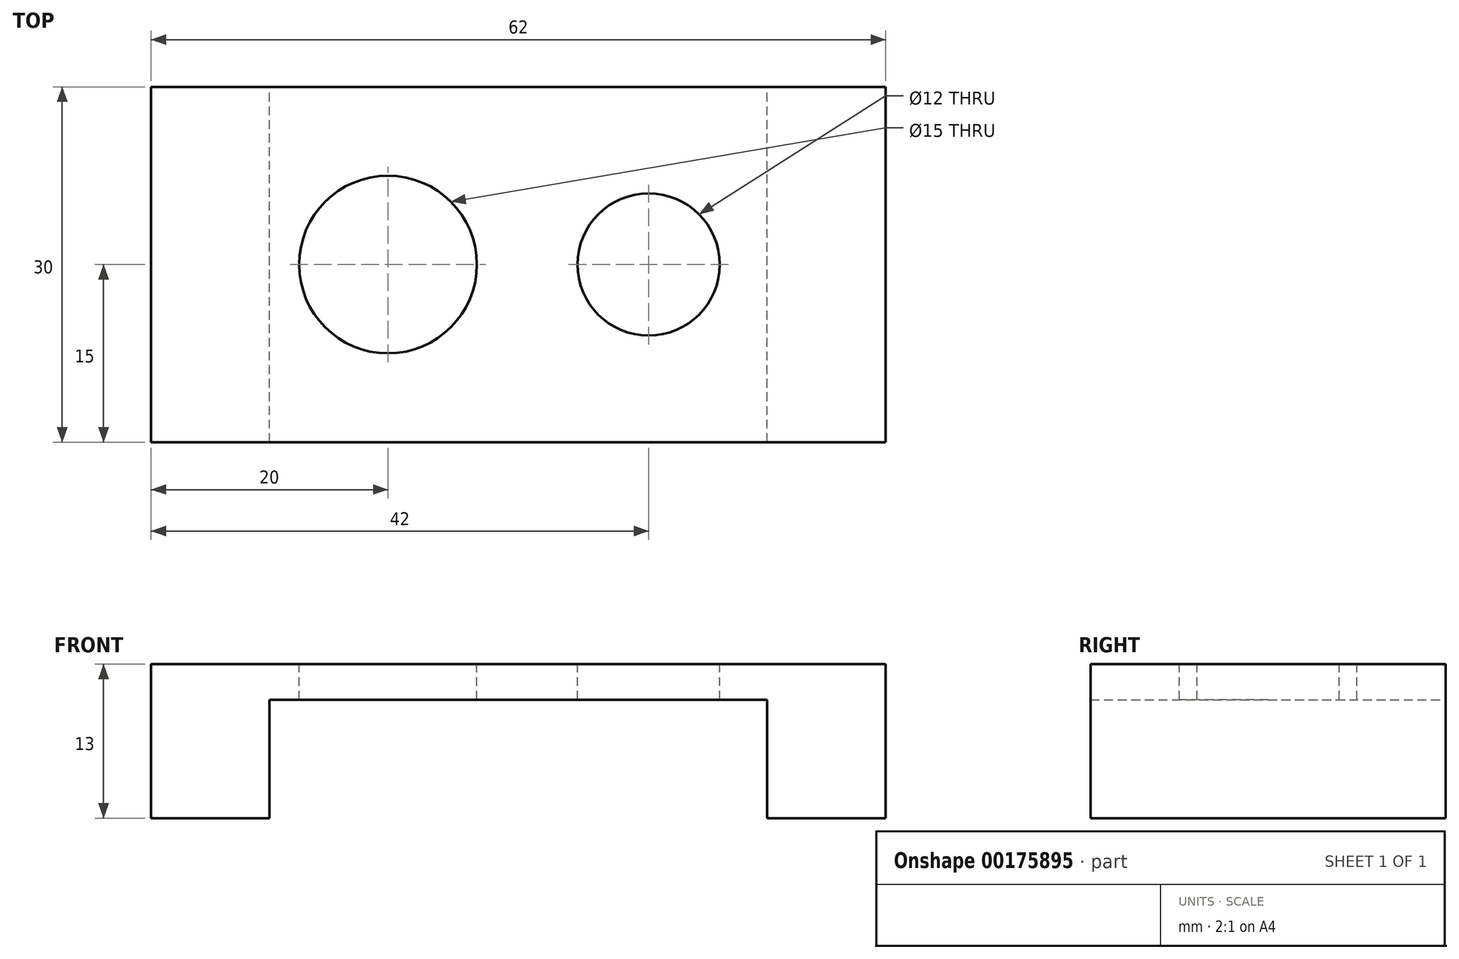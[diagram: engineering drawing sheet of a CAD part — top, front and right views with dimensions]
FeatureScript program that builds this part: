
annotation { "Feature Type Name" : "Feature", "Feature Type Description" : "" }
export const myFeature = defineFeature(function(context is Context, id is Id, definition is map)
    precondition{}
    {
        {
            var Q0;
            Q0=qCreatedBy(makeId("Front.planeOp"),FACE);
            var sketch = newSketch(context, id + "F0", { "sketchPlane" : qUnion([Q0])});
            skLineSegment(sketch, "E0", {"start": v(0, 0) * mm, "end": v(62, 0) * mm});
            skLineSegment(sketch, "E1", {"start": v(62, 0) * mm, "end": v(62, -13) * mm});
            skLineSegment(sketch, "E2", {"start": v(62, -13) * mm, "end": v(52, -13) * mm});
            skLineSegment(sketch, "E3", {"start": v(52, -13) * mm, "end": v(52, -3) * mm});
            skLineSegment(sketch, "E4", {"start": v(52, -3) * mm, "end": v(10, -3) * mm});
            skLineSegment(sketch, "E5", {"start": v(10, -3) * mm, "end": v(10, -13) * mm});
            skLineSegment(sketch, "E6", {"start": v(10, -13) * mm, "end": v(0, -13) * mm});
            skLineSegment(sketch, "E7", {"start": v(0, -13) * mm, "end": v(0, 0) * mm});
            skSolve(sketch);
        }
        {
            var Q0;
            Q0 = qSketchRegion(id + "F0", true);
            extrude(context, id + "F1", {"entities" : qUnion([Q0]), "depth" : 30 * mm});
        }
        {
            var Q0;
            Q0=qCreatedBy(makeId("Top.planeOp"),FACE);
            var sketch = newSketch(context, id + "F2", { "sketchPlane" : qUnion([Q0])});
            skCircle(sketch, "E8", {"center": v(20, -15) * mm, "radius": 7.5 * mm});
            skCircle(sketch, "E9", {"center": v(42, -15) * mm, "radius": 6 * mm});
            skSolve(sketch);
        }
        {
            var Q0;
            Q0 = qSketchRegion(id + "F2", true);
            extrude(context, id + "F3", {"entities" : qUnion([Q0]), "operationType" : NewBodyOperationType.REMOVE, "endBound" : BoundingType.THROUGH_ALL, "oppositeDirection" : true, "depth" : 25 * mm});
        }
    });
